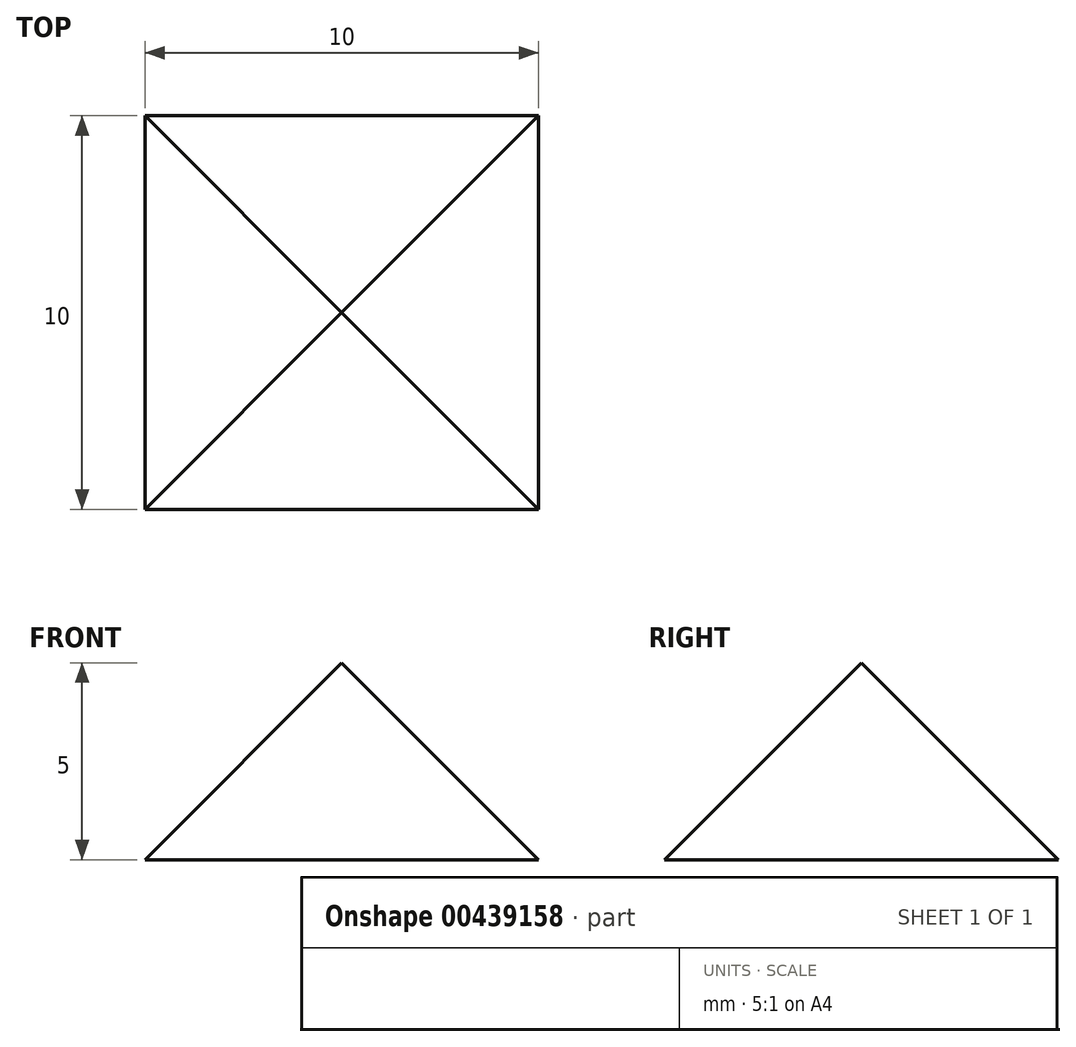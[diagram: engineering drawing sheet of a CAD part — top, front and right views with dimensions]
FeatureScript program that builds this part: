
annotation { "Feature Type Name" : "Feature", "Feature Type Description" : "" }
export const myFeature = defineFeature(function(context is Context, id is Id, definition is map)
    precondition{}
    {
        {
            var Q0;
            Q0=qCreatedBy(makeId("Top.planeOp"),FACE);
            var sketch = newSketch(context, id + "F0", { "sketchPlane" : qUnion([Q0])});
            skLineSegment(sketch, "E0.bottom", {"start": v(5, -5) * mm, "end": v(-5, -5) * mm});
            skLineSegment(sketch, "E0.top", {"start": v(5, 5) * mm, "end": v(-5, 5) * mm});
            skLineSegment(sketch, "E0.left", {"start": v(5, -5) * mm, "end": v(5, 5) * mm});
            skLineSegment(sketch, "E0.right", {"start": v(-5, -5) * mm, "end": v(-5, 5) * mm});
            skPoint(sketch, "E0.middle", {"position": v(0, 0) * mm});
            skSolve(sketch);
        }
        {
            var Q0;
            Q0 = qSketchRegion(id + "F0", true);
            extrude(context, id + "F1", {"entities" : qUnion([Q0]), "depth" : 5 * mm});
        }
        {
            var Q0;
            Q0=makeQuery(id+"F1.opExtrude","CAP_EDGE",EDGE,{"disambiguationData":[OSD([sQuery(id+"F0.wireOp",EDGE,"E0.right")])],"isStart":false});
            var Q1;
            Q1=makeQuery(id+"F1.opExtrude","CAP_EDGE",EDGE,{"disambiguationData":[OSD([sQuery(id+"F0.wireOp",EDGE,"E0.bottom")])],"isStart":false});
            var Q2;
            Q2=makeQuery(id+"F1.opExtrude","CAP_EDGE",EDGE,{"disambiguationData":[OSD([sQuery(id+"F0.wireOp",EDGE,"E0.left")])],"isStart":false});
            var Q3;
            Q3=makeQuery(id+"F1.opExtrude","CAP_EDGE",EDGE,{"disambiguationData":[OSD([sQuery(id+"F0.wireOp",EDGE,"E0.top")])],"isStart":false});
            chamfer(context, id + "F2", {"entities" : qUnion([Q0, Q1, Q2, Q3]), "width" : 5 * mm, "tangentPropagation" : true});
        }
    });
